FCSTD DOCUMENT  (FreeCAD 0.18R4 (GitTag))
Label: GPS
License: All rights reserved
LicenseURL: http://en.wikipedia.org/wiki/All_rights_reserved
objects: Sketcher::SketchObject×1, PartDesign::Body×1
note: 2 computed .brp shape members not serialized (recipe doc carries the construction recipe); baked Part::Feature solids carry a one-line shape summary decoded from their .brp

FEATURE [Sketcher::SketchObject] Sketch
  MapMode = 5
  Support = -> [XY_Plane]
  sketch-geometry (21):
    g0: LineSegment StartX=40 StartY=-48.225 StartZ=0 EndX=-40 EndY=-48.225 EndZ=0
    g1: LineSegment StartX=-40 StartY=-48.225 StartZ=0 EndX=-40 EndY=48.225 EndZ=0
    g2: Circle CenterX=37.5 CenterY=-45.725 CenterZ=0 NormalX=0 NormalY=0 NormalZ=1 AngleXU=0 Radius=1.5
    g3: Circle CenterX=-37.5 CenterY=-45.725 CenterZ=0 NormalX=0 NormalY=0 NormalZ=1 AngleXU=0 Radius=1.5
    g4: Circle CenterX=37.5 CenterY=-14.725 CenterZ=0 NormalX=0 NormalY=0 NormalZ=1 AngleXU=0 Radius=1.5
    g5: LineSegment StartX=40 StartY=-48.225 StartZ=0 EndX=40 EndY=-12.225 EndZ=0
    g6: LineSegment StartX=40 StartY=-12.225 StartZ=0 EndX=31 EndY=-12.225 EndZ=0
    g7: LineSegment StartX=31 StartY=48.225 StartZ=0 EndX=31 EndY=-12.225 EndZ=0
    g8: LineSegment StartX=-40 StartY=48.225 StartZ=0 EndX=31 EndY=48.225 EndZ=0
    g9: LineSegment StartX=-35.7 StartY=-19.425 StartZ=0 EndX=35.7 EndY=-19.425 EndZ=0
    g10: LineSegment StartX=35.7 StartY=-19.425 StartZ=0 EndX=35.7 EndY=-43.725 EndZ=0
    g11: LineSegment StartX=35.7 StartY=-43.725 StartZ=0 EndX=-35.7 EndY=-43.725 EndZ=0
    g12: LineSegment StartX=-35.7 StartY=-43.725 StartZ=0 EndX=-35.7 EndY=-19.425 EndZ=0
    g13: LineSegment StartX=21 StartY=12.275 StartZ=0 EndX=27.4 EndY=12.275 EndZ=0
    g14: LineSegment StartX=27.4 StartY=12.275 StartZ=0 EndX=27.4 EndY=4.675 EndZ=0
    g15: LineSegment StartX=27.4 StartY=4.675 StartZ=0 EndX=21 EndY=4.675 EndZ=0
    g16: LineSegment StartX=21 StartY=4.675 StartZ=0 EndX=21 EndY=12.275 EndZ=0
    g17: LineSegment StartX=-27.85 StartY=11.575 StartZ=0 EndX=-18.05 EndY=11.575 EndZ=0
    g18: LineSegment StartX=-18.05 StartY=11.575 StartZ=0 EndX=-18.05 EndY=0.375 EndZ=0
    g19: LineSegment StartX=-18.05 StartY=0.375 StartZ=0 EndX=-27.85 EndY=0.375 EndZ=0
    g20: LineSegment StartX=-27.85 StartY=0.375 StartZ=0 EndX=-27.85 EndY=11.575 EndZ=0
  constraints (61):
    c: Coincident(g0,g1)
    c: DistanceX(g0,g0) = 80
    c: Diameter(g2) = 3
    c: Distance(g2,g0) = 2.5
    c: Diameter(g3) = 3
    c: Distance(g3,g0) = 2.5
    c: Distance(g3,g1) = 2.5
    c: Diameter(g4) = 3
    c: Distance(g4,g2) = 31
    c: Coincident(g0,g5)
    c: Coincident(g5,g6)
    c: Parallel(g5,g-2)
    c: Distance(g4,g5) = 2.5
    c: Distance(g2,g5) = 2.5
    c: DistanceY(g5,g5) = 36
    c: Parallel(g6,g-1)
    c: DistanceX(g6,g6) = 9
    c: Coincident(g6,g7)
    c: Parallel(g7,g-2)
    c: Symmetric(g0,g0,g-2)
    c: Coincident(g1,g8)
    c: DistanceY(g1,g1) = 96.45
    c: Coincident(g7,g8)
    c: Parallel(g-1,g8)
    c: Coincident(g9,g10)
    c: Coincident(g10,g11)
    c: Coincident(g11,g12)
    c: Coincident(g12,g9)
    c: Horizontal(g9)
    c: Horizontal(g11)
    c: Vertical(g10)
    c: Vertical(g12)
    c: Distance(g9,g5) = 4.3
    c: Distance(g9,g1) = 4.3
    c: Distance(g10,g0) = 4.5
    c: DistanceY(g10,g10) = 24.3
    c: Coincident(g13,g14)
    c: Coincident(g14,g15)
    c: Coincident(g15,g16)
    c: Coincident(g16,g13)
    c: Horizontal(g13)
    c: Horizontal(g15)
    c: Vertical(g14)
    c: Vertical(g16)
    c: Symmetric(g0,g1,g-1)
    c: Distance(g13,g7) = 3.6
    c: DistanceX(g13,g13) = 6.4
    c: DistanceY(g14,g14) = 7.6
    c: Coincident(g17,g18)
    c: Coincident(g18,g19)
    c: Coincident(g19,g20)
    c: Coincident(g20,g17)
    c: Horizontal(g17)
    c: Horizontal(g19)
    c: Vertical(g18)
    c: Vertical(g20)
    c: DistanceX(g17,g17) = 9.8
    c: DistanceY(g18,g18) = 11.2
    c: Distance(g17,g1) = 12.15
    c: Distance(g13,g0) = 60.5
    c: Distance(g17,g0) = 59.8
FEATURE [PartDesign::Body] Body
  Group = -> [Sketch]
  Origin = -> Origin
